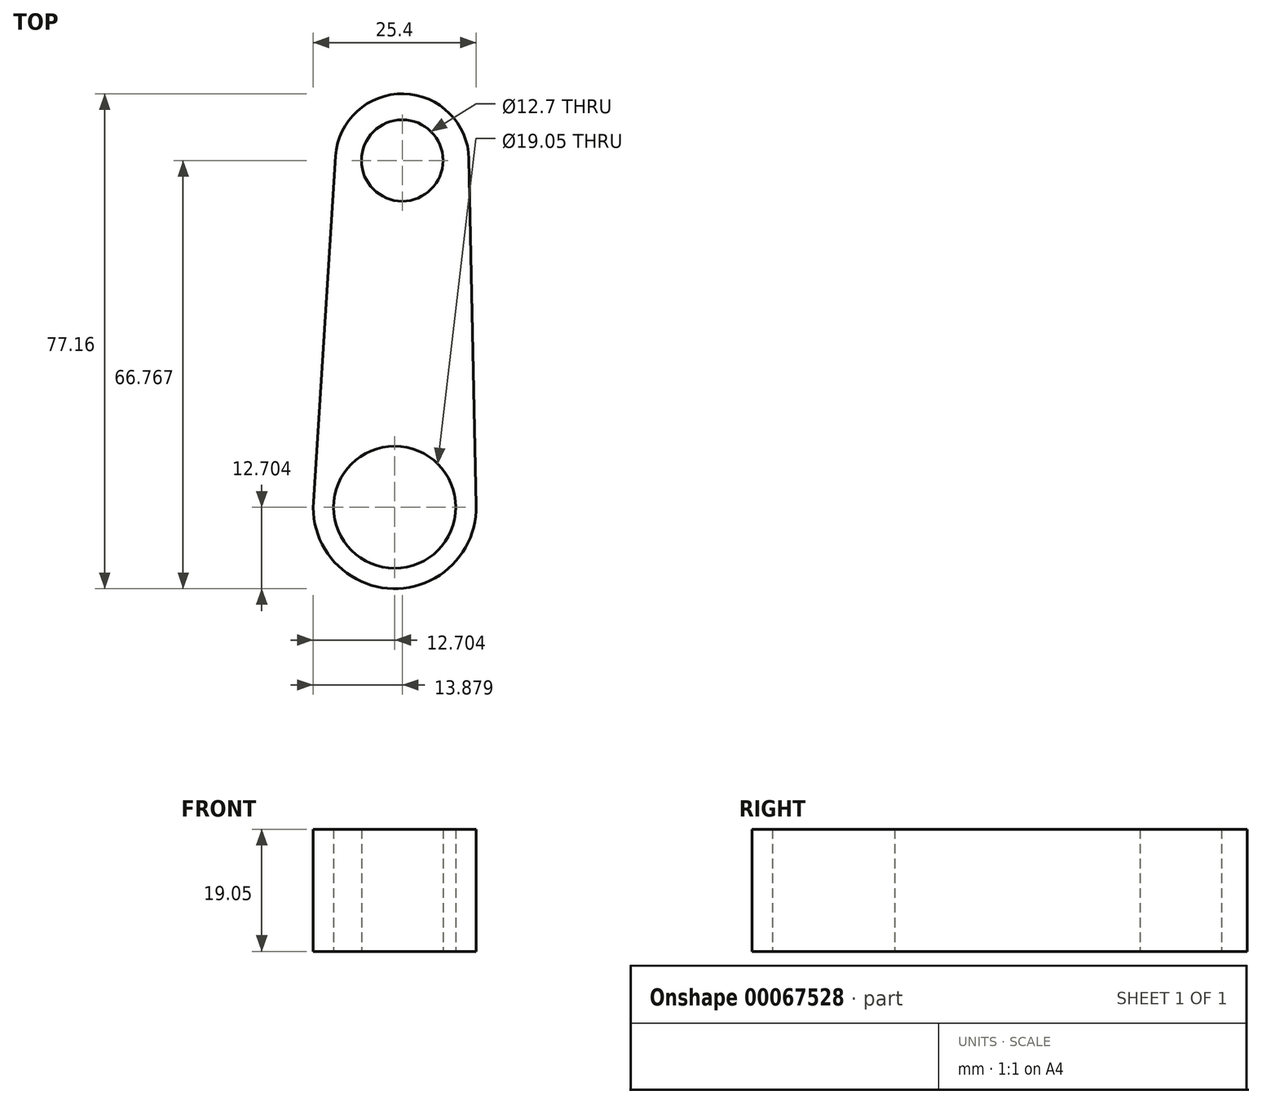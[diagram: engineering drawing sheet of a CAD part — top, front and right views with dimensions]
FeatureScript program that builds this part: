
annotation { "Feature Type Name" : "Feature", "Feature Type Description" : "" }
export const myFeature = defineFeature(function(context is Context, id is Id, definition is map)
    precondition{}
    {
        {
            var Q0;
            Q0=qCreatedBy(makeId("Top.planeOp"),FACE);
            var sketch = newSketch(context, id + "F0", { "sketchPlane" : qUnion([Q0])});
            skCircle(sketch, "E0", {"center": v(12.28, 14.43) * mm, "radius": 9.53 * mm});
            skCircle(sketch, "E1", {"center": v(12.28, 14.43) * mm, "radius": 12.7 * mm});
            skCircle(sketch, "E2", {"center": v(13.46, 68.5) * mm, "radius": 6.35 * mm});
            skCircle(sketch, "E3", {"center": v(13.46, 68.5) * mm, "radius": 10.4 * mm});
            skLineSegment(sketch, "E4", {"start": v(3.08, 69.17) * mm, "end": v(-0.4, 15.25) * mm});
            skLineSegment(sketch, "E5", {"start": v(23.85, 68.71) * mm, "end": v(24.98, 14.7) * mm});
            skSolve(sketch);
        }
        {
            var Q0;
            Q0=makeQuery(id+"F0.imprint","IMPRINT",FACE,{"disambiguationData":[TD([[makeQuery(id+"F0.imprint","IMPRINT",EDGE,{"derivedFrom":sQuery(id+"F0.wireOp",EDGE,"E2")}),-1.0]])]});
            var Q1;
            {var subQ0=sQuery(id+"F0.wireOp",EDGE,"E4");Q1=makeQuery(id+"F0.imprint","IMPRINT",FACE,{"disambiguationData":[TD([[makeQuery(id+"F0.imprint","IMPRINT",EDGE,{"derivedFrom":subQ0}),1.0]])]});}
            var Q2;
            Q2=makeQuery(id+"F0.imprint","IMPRINT",FACE,{"disambiguationData":[TD([[makeQuery(id+"F0.imprint","IMPRINT",EDGE,{"derivedFrom":sQuery(id+"F0.wireOp",EDGE,"E0")}),-1.0]])]});
            extrude(context, id + "F1", {"entities" : qUnion([Q0, Q1, Q2]), "depth" : 19.05 * mm});
        }
    });
